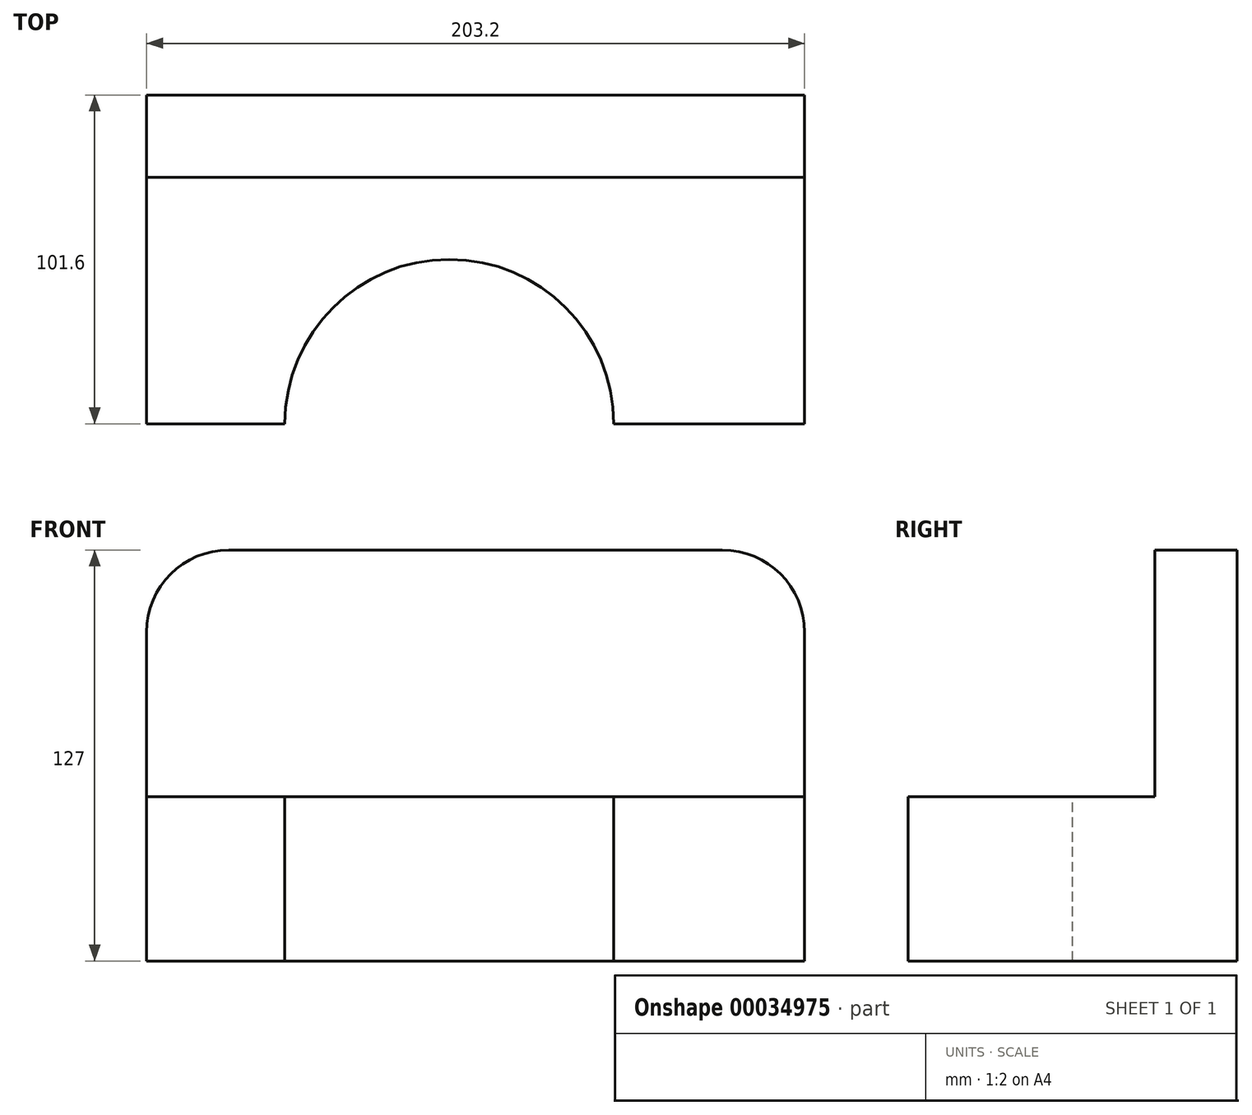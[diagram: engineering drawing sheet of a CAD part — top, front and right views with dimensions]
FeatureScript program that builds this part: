
annotation { "Feature Type Name" : "Feature", "Feature Type Description" : "" }
export const myFeature = defineFeature(function(context is Context, id is Id, definition is map)
    precondition{}
    {
        {
            var Q0;
            Q0=qCreatedBy(makeId("Top.planeOp"),FACE);
            var sketch = newSketch(context, id + "F8", { "sketchPlane" : qUnion([Q0])});
            skLineSegment(sketch, "E0.bottom", {"start": v(-45.93, 38.77) * mm, "end": v(157.27, 38.77) * mm});
            skLineSegment(sketch, "E0.top", {"start": v(-45.93, -62.83) * mm, "end": v(157.27, -62.83) * mm});
            skLineSegment(sketch, "E0.left", {"start": v(-45.93, 38.77) * mm, "end": v(-45.93, -62.83) * mm});
            skLineSegment(sketch, "E0.right", {"start": v(157.27, 38.77) * mm, "end": v(157.27, -62.83) * mm});
            skSolve(sketch);
        }
        {
            var Q0;
            Q0 = qSketchRegion(id + "F8", true);
            var Q1;
            Q1=makeQuery(id+"F8.imprint","IMPRINT",FACE,{"disambiguationData":[TD([[makeQuery(id+"F8.imprint","IMPRINT",EDGE,{"derivedFrom":sQuery(id+"F8.wireOp",EDGE,"E0.bottom")}),-1.0]])]});
            extrude(context, id + "F0", {"entities" : qUnion([Q0, Q1]), "depth" : 25.4 * mm});
        }
        {
            var Q0;
            Q0=makeQuery(id+"F0.opExtrude","CAP_FACE",FACE,{"disambiguationData":[OSD([sQuery(id+"F8.wireOp",EDGE,"E0.bottom"),sQuery(id+"F8.wireOp",EDGE,"E0.top"),sQuery(id+"F8.wireOp",EDGE,"E0.left"),sQuery(id+"F8.wireOp",EDGE,"E0.right")])],"isStart":false});
            var sketch = newSketch(context, id + "F1", { "sketchPlane" : qUnion([Q0])});
            skLineSegment(sketch, "E1.bottom", {"start": v(-45.93, 38.77) * mm, "end": v(157.27, 38.77) * mm});
            skLineSegment(sketch, "E1.top", {"start": v(-45.93, 13.37) * mm, "end": v(157.27, 13.37) * mm});
            skLineSegment(sketch, "E1.left", {"start": v(-45.93, 38.77) * mm, "end": v(-45.93, 13.37) * mm});
            skLineSegment(sketch, "E1.right", {"start": v(157.27, 38.77) * mm, "end": v(157.27, 13.37) * mm});
            skSolve(sketch);
        }
        {
            var Q0;
            Q0 = qSketchRegion(id + "F1", true);
            var Q1;
            Q1=makeQuery(id+"F1.imprint","IMPRINT",FACE,{"disambiguationData":[TD([[makeQuery(id+"F1.imprint","IMPRINT",EDGE,{"derivedFrom":sQuery(id+"F1.wireOp",EDGE,"E1.bottom")}),-1.0]])]});
            extrude(context, id + "F2", {"entities" : qUnion([Q0, Q1]), "operationType" : NewBodyOperationType.ADD, "depth" : 101.6 * mm});
        }
        {
            var Q0;
            Q0=makeQuery(id+"F2.opExtrude","SWEPT_FACE",FACE,{"disambiguationData":[OSD([sQuery(id+"F1.wireOp",EDGE,"E1.top")])]});
            var sketch = newSketch(context, id + "F3", { "sketchPlane" : qUnion([Q0])});
            skLineSegment(sketch, "E2", {"start": v(157.27, 127) * mm, "end": v(131.87, 127) * mm});
            skLineSegment(sketch, "E3", {"start": v(131.87, 127) * mm, "end": v(131.87, 101.6) * mm});
            skCircle(sketch, "E4", {"center": v(131.87, 101.6) * mm, "radius": 25.4 * mm});
            skSolve(sketch);
        }
        {
            var Q0;
            {var subQ4=sQuery(id+"F3.wireOp",EDGE,"E2");Q0=makeQuery(id+"F3.imprint","IMPRINT",FACE,{"disambiguationData":[TD([[makeQuery(id+"F3.imprint","IMPRINT",EDGE,{"derivedFrom":subQ4}),-1.0]])]});}
            extrude(context, id + "F9", {"entities" : qUnion([Q0]), "operationType" : NewBodyOperationType.REMOVE, "oppositeDirection" : true, "depth" : 25.4 * mm});
        }
        {
            var Q0;
            Q0=makeQuery(id+"F2.opExtrude","CAP_EDGE",EDGE,{"disambiguationData":[OSD([sQuery(id+"F1.wireOp",EDGE,"E1.left")])],"isStart":false});
            fillet(context, id + "F4", {"entities" : qUnion([Q0]), "radius" : 25.4 * mm, "tangentPropagation" : true, "allowEdgeOverflow" : false});
        }
        {
            var Q0;
            Q0=makeQuery(id+"F0.opExtrude","CAP_FACE",FACE,{"disambiguationData":[OSD([sQuery(id+"F8.wireOp",EDGE,"E0.bottom"),sQuery(id+"F8.wireOp",EDGE,"E0.top"),sQuery(id+"F8.wireOp",EDGE,"E0.left"),sQuery(id+"F8.wireOp",EDGE,"E0.right")])],"isStart":false});
            var sketch = newSketch(context, id + "F5", { "sketchPlane" : qUnion([Q0])});
            skCircle(sketch, "E5", {"center": v(47.56, -62.83) * mm, "radius": 50.8 * mm});
            skSolve(sketch);
        }
        {
            var Q0;
            Q0 = qSketchRegion(id + "F5", true);
            extrude(context, id + "F6", {"entities" : qUnion([Q0]), "operationType" : NewBodyOperationType.REMOVE, "oppositeDirection" : true, "depth" : 25.4 * mm});
        }
        {
            var Q0;
            Q0=makeQuery(id+"F0.opExtrude","CAP_FACE",FACE,{"disambiguationData":[OSD([sQuery(id+"F8.wireOp",EDGE,"E0.bottom"),sQuery(id+"F8.wireOp",EDGE,"E0.top"),sQuery(id+"F8.wireOp",EDGE,"E0.left"),sQuery(id+"F8.wireOp",EDGE,"E0.right")])],"isStart":false});
            extrude(context, id + "F7", {"entities" : qUnion([Q0]), "operationType" : NewBodyOperationType.ADD, "depth" : 25.4 * mm});
        }
    });
